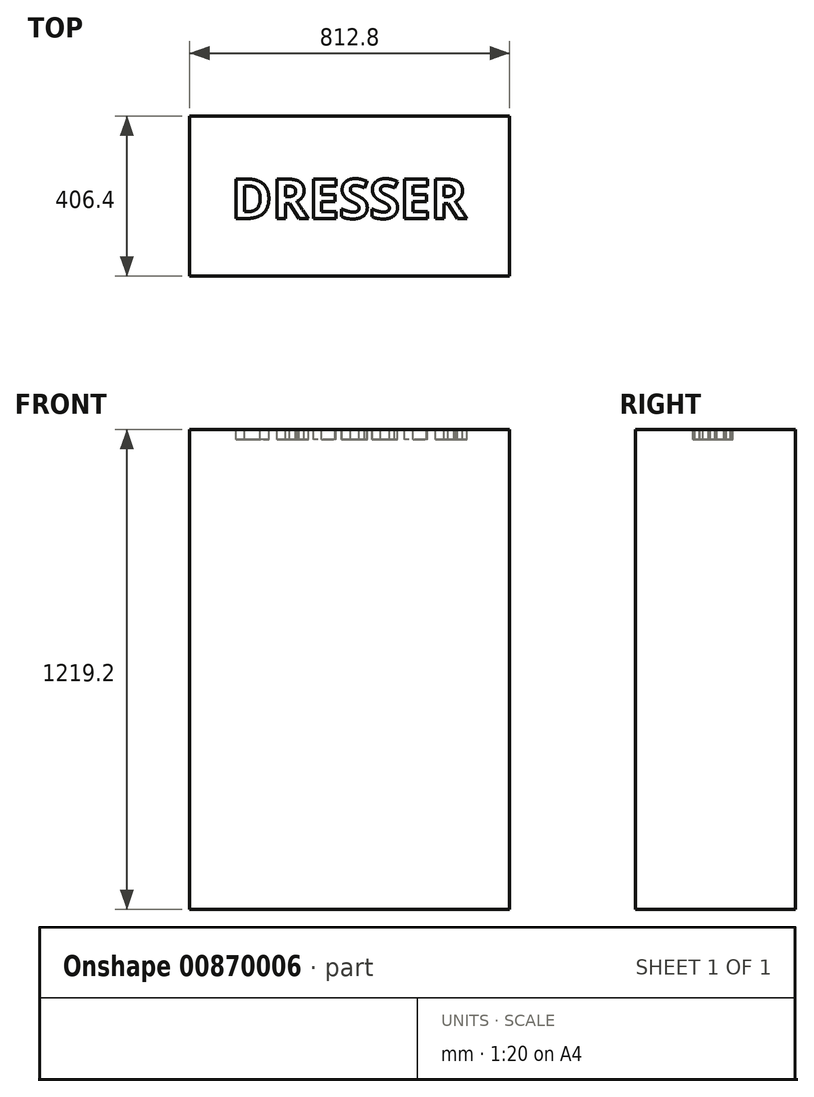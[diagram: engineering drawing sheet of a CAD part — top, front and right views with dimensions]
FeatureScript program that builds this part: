
annotation { "Feature Type Name" : "Feature", "Feature Type Description" : "" }
export const myFeature = defineFeature(function(context is Context, id is Id, definition is map)
    precondition{}
    {
        {
            var Q0;
            Q0=qCreatedBy(makeId("Top.planeOp"),FACE);
            var sketch = newSketch(context, id + "F0", { "sketchPlane" : qUnion([Q0])});
            skLineSegment(sketch, "E0.bottom", {"start": v(0, 0) * mm, "end": v(812.8, 0) * mm});
            skLineSegment(sketch, "E0.top", {"start": v(0, 406.4) * mm, "end": v(812.8, 406.4) * mm});
            skLineSegment(sketch, "E0.left", {"start": v(0, 0) * mm, "end": v(0, 406.4) * mm});
            skLineSegment(sketch, "E0.right", {"start": v(812.8, 0) * mm, "end": v(812.8, 406.4) * mm});
            skSolve(sketch);
        }
        {
            var Q0;
            Q0 = qSketchRegion(id + "F0", true);
            extrude(context, id + "F1", {"entities" : qUnion([Q0]), "depth" : 1219.2 * mm, "offsetDistance" : 25.4 * mm});
        }
        {
            var Q0;
            Q0=makeQuery(id+"F1.opExtrude","CAP_FACE",FACE,{"disambiguationData":[OSD([sQuery(id+"F0.wireOp",EDGE,"E0.bottom"),sQuery(id+"F0.wireOp",EDGE,"E0.top"),sQuery(id+"F0.wireOp",EDGE,"E0.left"),sQuery(id+"F0.wireOp",EDGE,"E0.right")])],"isStart":false});
            var sketch = newSketch(context, id + "F2", { "sketchPlane" : qUnion([Q0])});
            skText(sketch, "E1", { "text": "DRESSER", "fontName": "OpenSans-Bold.ttf"});
            const initialGuessF2  = {"E1": [0.10552, 0.14638, 1, 0, 0.1006]};
            skSetInitialGuess(sketch, initialGuessF2);
            skSolve(sketch);
        }
        {
            var Q0;
            Q0 = qSketchRegion(id + "F2", true);
            extrude(context, id + "F3", {"entities" : qUnion([Q0]), "operationType" : NewBodyOperationType.REMOVE, "oppositeDirection" : true, "depth" : 25.4 * mm, "offsetDistance" : 25.4 * mm});
        }
    });
